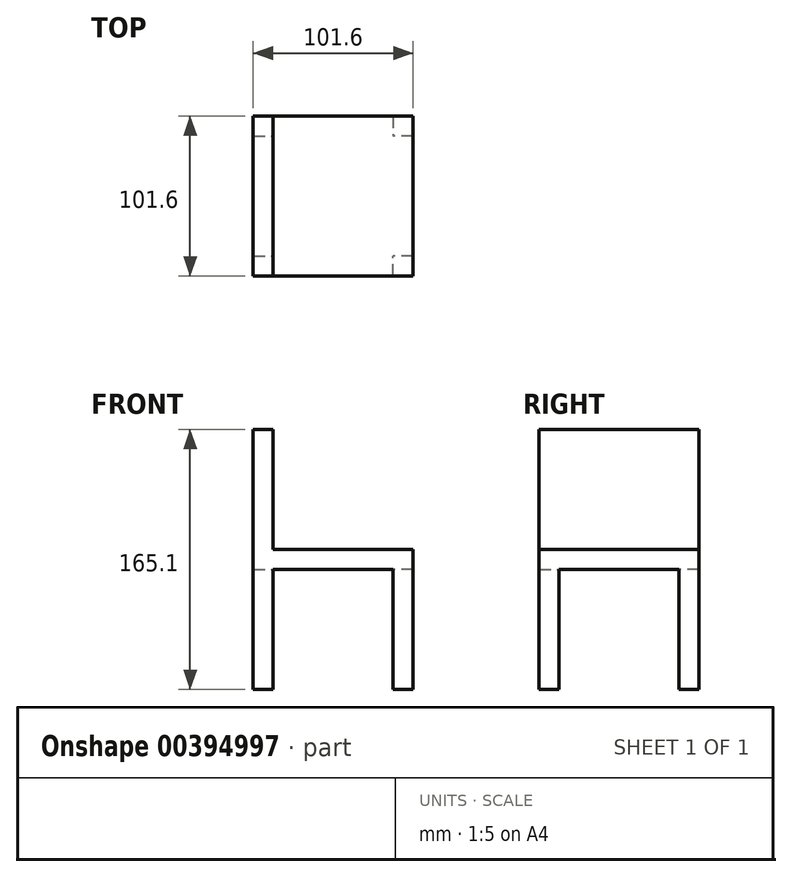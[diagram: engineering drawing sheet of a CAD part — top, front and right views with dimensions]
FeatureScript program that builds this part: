
annotation { "Feature Type Name" : "Feature", "Feature Type Description" : "" }
export const myFeature = defineFeature(function(context is Context, id is Id, definition is map)
    precondition{}
    {
        {
            var Q0;
            Q0=qCreatedBy(makeId("Top.planeOp"),FACE);
            var sketch = newSketch(context, id + "F0", { "sketchPlane" : qUnion([Q0])});
            skLineSegment(sketch, "E0.bottom", {"start": v(0, 0.8) * mm, "end": v(-101.6, 0.8) * mm});
            skLineSegment(sketch, "E0.top", {"start": v(0, 102.4) * mm, "end": v(-101.6, 102.4) * mm});
            skLineSegment(sketch, "E0.left", {"start": v(0, 0.8) * mm, "end": v(0, 102.4) * mm});
            skLineSegment(sketch, "E0.right", {"start": v(-101.6, 0.8) * mm, "end": v(-101.6, 102.4) * mm});
            skSolve(sketch);
        }
        {
            var Q0;
            Q0=makeQuery(id+"F0.imprint","IMPRINT",FACE,{"disambiguationData":[TD([[makeQuery(id+"F0.imprint","IMPRINT",EDGE,{"derivedFrom":sQuery(id+"F0.wireOp",EDGE,"E0.bottom")}),-1.0]])]});
            extrude(context, id + "F1", {"entities" : qUnion([Q0]), "depth" : 12.7 * mm});
        }
        {
            var Q0;
            Q0=makeQuery(id+"F1.opExtrude","CAP_FACE",FACE,{"disambiguationData":[OSD([sQuery(id+"F0.wireOp",EDGE,"E0.bottom"),sQuery(id+"F0.wireOp",EDGE,"E0.top"),sQuery(id+"F0.wireOp",EDGE,"E0.left"),sQuery(id+"F0.wireOp",EDGE,"E0.right")])],"isStart":true});
            var sketch = newSketch(context, id + "F2", { "sketchPlane" : qUnion([Q0])});
            skLineSegment(sketch, "E1.bottom", {"start": v(-101.6, -0.8) * mm, "end": v(-88.9, -0.8) * mm});
            skLineSegment(sketch, "E1.top", {"start": v(-101.6, -13.5) * mm, "end": v(-88.9, -13.5) * mm});
            skLineSegment(sketch, "E1.left", {"start": v(-101.6, -0.8) * mm, "end": v(-101.6, -13.5) * mm});
            skLineSegment(sketch, "E1.right", {"start": v(-88.9, -0.8) * mm, "end": v(-88.9, -13.5) * mm});
            skLineSegment(sketch, "E2.bottom", {"start": v(0, -0.8) * mm, "end": v(-12.7, -0.8) * mm});
            skLineSegment(sketch, "E2.top", {"start": v(0, -13.5) * mm, "end": v(-12.7, -13.5) * mm});
            skLineSegment(sketch, "E2.left", {"start": v(0, -0.8) * mm, "end": v(0, -13.5) * mm});
            skLineSegment(sketch, "E2.right", {"start": v(-12.7, -0.8) * mm, "end": v(-12.7, -13.5) * mm});
            skLineSegment(sketch, "E3.bottom", {"start": v(0, -102.4) * mm, "end": v(-12.7, -102.4) * mm});
            skLineSegment(sketch, "E3.top", {"start": v(0, -89.7) * mm, "end": v(-12.7, -89.7) * mm});
            skLineSegment(sketch, "E3.left", {"start": v(0, -102.4) * mm, "end": v(0, -89.7) * mm});
            skLineSegment(sketch, "E3.right", {"start": v(-12.7, -102.4) * mm, "end": v(-12.7, -89.7) * mm});
            skLineSegment(sketch, "E4.bottom", {"start": v(-101.6, -102.4) * mm, "end": v(-88.9, -102.4) * mm});
            skLineSegment(sketch, "E4.top", {"start": v(-101.6, -89.7) * mm, "end": v(-88.9, -89.7) * mm});
            skLineSegment(sketch, "E4.left", {"start": v(-101.6, -102.4) * mm, "end": v(-101.6, -89.7) * mm});
            skLineSegment(sketch, "E4.right", {"start": v(-88.9, -102.4) * mm, "end": v(-88.9, -89.7) * mm});
            skSolve(sketch);
        }
        {
            var Q0;
            Q0=makeQuery(id+"F2.imprint","IMPRINT",FACE,{"disambiguationData":[TD([[makeQuery(id+"F2.imprint","IMPRINT",EDGE,{"derivedFrom":sQuery(id+"F2.wireOp",EDGE,"E1.bottom")}),1.0]])]});
            var Q1;
            Q1=makeQuery(id+"F2.imprint","IMPRINT",FACE,{"disambiguationData":[TD([[makeQuery(id+"F2.imprint","IMPRINT",EDGE,{"derivedFrom":sQuery(id+"F2.wireOp",EDGE,"E2.bottom")}),1.0]])]});
            var Q2;
            Q2=makeQuery(id+"F2.imprint","IMPRINT",FACE,{"disambiguationData":[TD([[makeQuery(id+"F2.imprint","IMPRINT",EDGE,{"derivedFrom":sQuery(id+"F2.wireOp",EDGE,"E3.bottom")}),-1.0]])]});
            var Q3;
            Q3=makeQuery(id+"F2.imprint","IMPRINT",FACE,{"disambiguationData":[TD([[makeQuery(id+"F2.imprint","IMPRINT",EDGE,{"derivedFrom":sQuery(id+"F2.wireOp",EDGE,"E4.bottom")}),-1.0]])]});
            extrude(context, id + "F3", {"entities" : qUnion([Q0, Q1, Q2, Q3]), "operationType" : NewBodyOperationType.ADD, "depth" : 76.2 * mm});
        }
        {
            var Q0;
            Q0=makeQuery(id+"F1.opExtrude","CAP_FACE",FACE,{"disambiguationData":[OSD([sQuery(id+"F0.wireOp",EDGE,"E0.bottom"),sQuery(id+"F0.wireOp",EDGE,"E0.top"),sQuery(id+"F0.wireOp",EDGE,"E0.left"),sQuery(id+"F0.wireOp",EDGE,"E0.right")])],"isStart":false});
            var sketch = newSketch(context, id + "F4", { "sketchPlane" : qUnion([Q0])});
            skLineSegment(sketch, "E5.bottom", {"start": v(-101.6, 102.4) * mm, "end": v(-88.9, 102.4) * mm});
            skLineSegment(sketch, "E5.top", {"start": v(-101.6, 0.8) * mm, "end": v(-88.9, 0.8) * mm});
            skLineSegment(sketch, "E5.left", {"start": v(-101.6, 102.4) * mm, "end": v(-101.6, 0.8) * mm});
            skLineSegment(sketch, "E5.right", {"start": v(-88.9, 102.4) * mm, "end": v(-88.9, 0.8) * mm});
            skSolve(sketch);
        }
        {
            var Q0;
            Q0=makeQuery(id+"F4.imprint","IMPRINT",FACE,{"disambiguationData":[TD([[makeQuery(id+"F4.imprint","IMPRINT",EDGE,{"derivedFrom":sQuery(id+"F4.wireOp",EDGE,"E5.bottom")}),1.0]])]});
            extrude(context, id + "F5", {"entities" : qUnion([Q0]), "operationType" : NewBodyOperationType.ADD, "depth" : 76.2 * mm});
        }
    });
